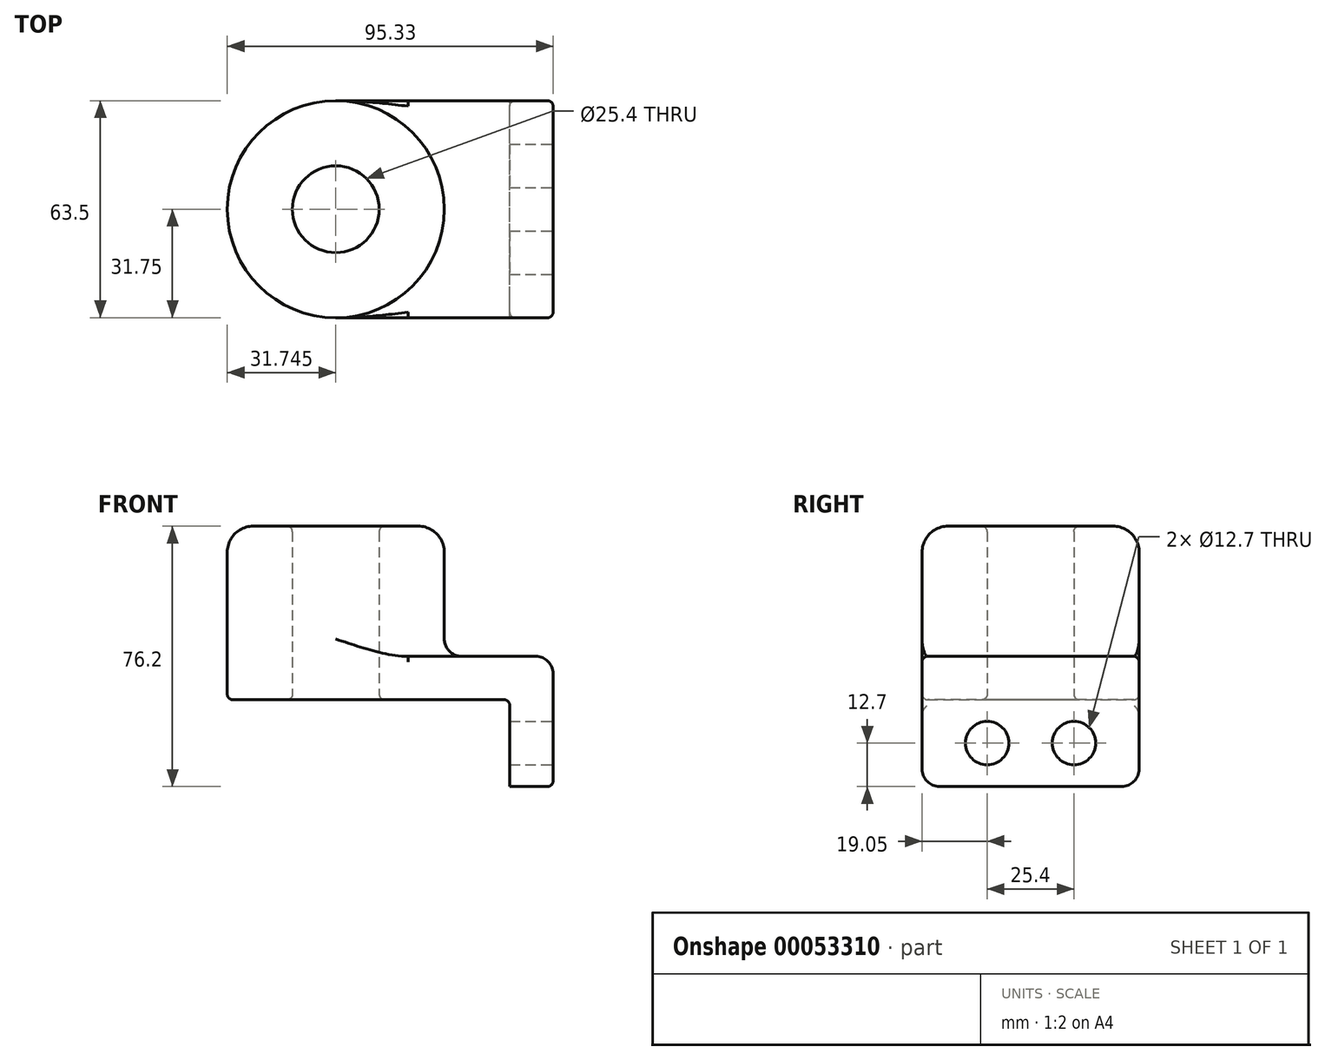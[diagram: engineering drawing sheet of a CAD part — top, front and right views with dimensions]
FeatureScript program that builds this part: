
annotation { "Feature Type Name" : "Feature", "Feature Type Description" : "" }
export const myFeature = defineFeature(function(context is Context, id is Id, definition is map)
    precondition{}
    {
        {
            var Q0;
            Q0=qCreatedBy(makeId("Top.planeOp"),FACE);
            var sketch = newSketch(context, id + "F0", { "sketchPlane" : qUnion([Q0])});
            skLineSegment(sketch, "E0.bottom", {"start": v(31.8, -31.75) * mm, "end": v(-31.8, -31.75) * mm});
            skLineSegment(sketch, "E0.top", {"start": v(31.8, 31.75) * mm, "end": v(-31.8, 31.75) * mm});
            skLineSegment(sketch, "E0.left", {"start": v(31.8, -31.75) * mm, "end": v(31.8, 31.75) * mm});
            skLineSegment(sketch, "E0.right", {"start": v(-31.8, -31.75) * mm, "end": v(-31.8, 31.75) * mm});
            skPoint(sketch, "E0.middle", {"position": v(0, 0) * mm});
            skCircle(sketch, "E1", {"center": v(-31.8, 0) * mm, "radius": 31.75 * mm});
            skCircle(sketch, "E2", {"center": v(-31.8, 0) * mm, "radius": 12.7 * mm});
            skSolve(sketch);
        }
        {
            var Q0;
            Q0 = qSketchRegion(id + "F0", true);
            extrude(context, id + "F1", {"entities" : qUnion([Q0]), "depth" : 12.7 * mm});
        }
        {
            var Q0;
            {var subQ1=sQuery(id+"F0.wireOp",EDGE,"E0.right");var subQ3=sQuery(id+"F0.wireOp",EDGE,"E2");var subQ4=makeQuery(id+"F0.imprint","INTERSECT",VERTEX,{"disambiguationData":[OD(0.0)],"derivedFrom":[subQ1,subQ3]});Q0=makeQuery(id+"F0.imprint","IMPRINT",FACE,{"disambiguationData":[TD([[makeQuery(id+"F0.imprint","IMPRINT",EDGE,{"disambiguationData":[TD([[subQ4,1.0]])],"derivedFrom":subQ3}),-1.0]])]});}
            var Q1;
            {var subQ1=sQuery(id+"F0.wireOp",EDGE,"E0.right");var subQ3=sQuery(id+"F0.wireOp",EDGE,"E2");var subQ4=makeQuery(id+"F0.imprint","INTERSECT",VERTEX,{"disambiguationData":[OD(0.0)],"derivedFrom":[subQ1,subQ3]});Q1=makeQuery(id+"F0.imprint","IMPRINT",FACE,{"disambiguationData":[TD([[makeQuery(id+"F0.imprint","IMPRINT",EDGE,{"disambiguationData":[TD([[subQ4,-1.0]])],"derivedFrom":subQ3}),-1.0]])]});}
            extrude(context, id + "F2", {"entities" : qUnion([Q0, Q1]), "operationType" : NewBodyOperationType.ADD, "depth" : 50.8 * mm});
        }
        {
            var Q0;
            Q0=makeQuery(id+"F1.opExtrude","SWEPT_FACE",FACE,{"disambiguationData":[OSD([sQuery(id+"F0.wireOp",EDGE,"E0.left")])]});
            var sketch = newSketch(context, id + "F3", { "sketchPlane" : qUnion([Q0])});
            skLineSegment(sketch, "E3.bottom", {"start": v(-31.75, 12.7) * mm, "end": v(31.75, 12.7) * mm});
            skLineSegment(sketch, "E3.top", {"start": v(-31.75, -25.4) * mm, "end": v(31.75, -25.4) * mm});
            skLineSegment(sketch, "E3.left", {"start": v(-31.75, 12.7) * mm, "end": v(-31.75, -25.4) * mm});
            skLineSegment(sketch, "E3.right", {"start": v(31.75, 12.7) * mm, "end": v(31.75, -25.4) * mm});
            skCircle(sketch, "E4", {"center": v(-12.7, -12.7) * mm, "radius": 6.35 * mm});
            skLineSegment(sketch, "E5", {"start": v(0, 0) * mm, "end": v(0, -25.4) * mm});
            skCircle(sketch, "E6.MirrorC", {"center": v(12.7, -12.7) * mm, "radius": 6.35 * mm});
            skSolve(sketch);
        }
        {
            var Q0;
            Q0 = qSketchRegion(id + "F3", true);
            extrude(context, id + "F4", {"entities" : qUnion([Q0]), "operationType" : NewBodyOperationType.ADD, "oppositeDirection" : true, "depth" : 12.7 * mm});
        }
        {
            var Q0;
            {var subQ0=sQuery(id+"F0.wireOp",EDGE,"E1");Q0=makeQuery(id+"F2.boolean.opBoolean","INTERSECT",EDGE,{"derivedFrom":[makeQuery(id+"F1.opExtrude","CAP_FACE",FACE,{"disambiguationData":[OSD([sQuery(id+"F0.wireOp",EDGE,"E0.bottom"),sQuery(id+"F0.wireOp",EDGE,"E0.top"),sQuery(id+"F0.wireOp",EDGE,"E0.left"),subQ0,sQuery(id+"F0.wireOp",EDGE,"E2")])],"isStart":false}),makeQuery(id+"F2.opExtrude","SWEPT_FACE",FACE,{"disambiguationData":[OSD([subQ0])]})]});}
            var Q1;
            Q1=makeQuery(id+"F1.opExtrude","CAP_EDGE",EDGE,{"disambiguationData":[OSD([sQuery(id+"F0.wireOp",EDGE,"E0.left")])],"isStart":false});
            var Q2;
            Q2=makeQuery(id+"F4.opExtrude","SWEPT_EDGE",EDGE,{"disambiguationData":[OSD([sQuery(id+"F3.wireOp",EDGE,"E3.top"),sQuery(id+"F3.wireOp",EDGE,"E3.left")])]});
            var Q3;
            Q3=makeQuery(id+"F4.opExtrude","SWEPT_EDGE",EDGE,{"disambiguationData":[OSD([sQuery(id+"F3.wireOp",EDGE,"E3.top"),sQuery(id+"F3.wireOp",EDGE,"E3.right")])]});
            fillet(context, id + "F5", {"entities" : qUnion([Q0, Q1, Q2, Q3]), "radius" : 5.08 * mm, "tangentPropagation" : true, "allowEdgeOverflow" : false});
        }
        {
            var Q0;
            {var subQ0=sQuery(id+"F0.wireOp",EDGE,"E0.bottom");var subQ1=sQuery(id+"F0.wireOp",EDGE,"E1");Q0=makeQuery(id+"F5.opFillet","BLEND_EDGE",EDGE,{"blendedFrom":[makeQuery(id+"F2.boolean.opBoolean","INTERSECT",EDGE,{"derivedFrom":[makeQuery(id+"F1.opExtrude","CAP_FACE",FACE,{"disambiguationData":[OSD([subQ0,sQuery(id+"F0.wireOp",EDGE,"E0.top"),sQuery(id+"F0.wireOp",EDGE,"E0.left"),subQ1,sQuery(id+"F0.wireOp",EDGE,"E2")])],"isStart":false}),makeQuery(id+"F2.opExtrude","SWEPT_FACE",FACE,{"disambiguationData":[OSD([subQ1])]})]}),makeQuery(id+"F4.boolean.opBoolean","MERGE",FACE,{"derivedFrom":[makeQuery(id+"F1.opExtrude","SWEPT_FACE",FACE,{"disambiguationData":[OSD([subQ0])]}),makeQuery(id+"F4.opExtrude","SWEPT_FACE",FACE,{"disambiguationData":[OSD([sQuery(id+"F3.wireOp",EDGE,"E3.left")])]})]})],"blendedInto":[makeQuery(id+"F4.boolean.opBoolean","MERGE",FACE,{"derivedFrom":[makeQuery(id+"F1.opExtrude","SWEPT_FACE",FACE,{"disambiguationData":[OSD([subQ0])]}),makeQuery(id+"F4.opExtrude","SWEPT_FACE",FACE,{"disambiguationData":[OSD([sQuery(id+"F3.wireOp",EDGE,"E3.left")])]})]})]});}
            var Q1;
            Q1=makeQuery(id+"F1.opExtrude","CAP_EDGE",EDGE,{"disambiguationData":[OSD([sQuery(id+"F0.wireOp",EDGE,"E0.bottom")])],"isStart":false});
            var Q2;
            Q2=makeQuery(id+"F4.boolean.opBoolean","INTERSECT",EDGE,{"derivedFrom":[makeQuery(id+"F1.opExtrude","CAP_FACE",FACE,{"disambiguationData":[OSD([sQuery(id+"F0.wireOp",EDGE,"E0.bottom"),sQuery(id+"F0.wireOp",EDGE,"E0.top"),sQuery(id+"F0.wireOp",EDGE,"E0.left"),sQuery(id+"F0.wireOp",EDGE,"E1"),sQuery(id+"F0.wireOp",EDGE,"E2")])],"isStart":true}),makeQuery(id+"F4.opExtrude","CAP_FACE",FACE,{"disambiguationData":[OSD([sQuery(id+"F3.wireOp",EDGE,"E3.bottom"),sQuery(id+"F3.wireOp",EDGE,"E3.top"),sQuery(id+"F3.wireOp",EDGE,"E3.left"),sQuery(id+"F3.wireOp",EDGE,"E3.right"),sQuery(id+"F3.wireOp",EDGE,"E4"),sQuery(id+"F3.wireOp",EDGE,"E6.MirrorC")])],"isStart":false})]});
            var Q3;
            {var subQ0=sQuery(id+"F0.wireOp",EDGE,"E2");Q3=makeQuery(id+"F2.boolean.opBoolean","MERGE",FACE,{"derivedFrom":[makeQuery(id+"F1.opExtrude","SWEPT_FACE",FACE,{"disambiguationData":[OSD([subQ0])]}),makeQuery(id+"F2.opExtrude","SWEPT_FACE",FACE,{"disambiguationData":[OSD([subQ0])]})]});}
            var Q4;
            Q4=makeQuery(id+"F1.opExtrude","CAP_EDGE",EDGE,{"disambiguationData":[OSD([sQuery(id+"F0.wireOp",EDGE,"E0.top")])],"isStart":true});
            var Q5;
            Q5=makeQuery(id+"F1.opExtrude","CAP_EDGE",EDGE,{"disambiguationData":[OSD([sQuery(id+"F0.wireOp",EDGE,"E1")])],"isStart":true});
            fillet(context, id + "F6", {"entities" : qUnion([Q0, Q1, Q2, Q3, Q4, Q5]), "radius" : 1.59 * mm, "tangentPropagation" : true, "allowEdgeOverflow" : false});
        }
        {
            var Q0;
            Q0=makeQuery(id+"F2.opExtrude","CAP_EDGE",EDGE,{"disambiguationData":[OSD([sQuery(id+"F0.wireOp",EDGE,"E1")])],"isStart":false});
            fillet(context, id + "F7", {"entities" : qUnion([Q0]), "radius" : 7.62 * mm, "tangentPropagation" : true, "allowEdgeOverflow" : false});
        }
    });
